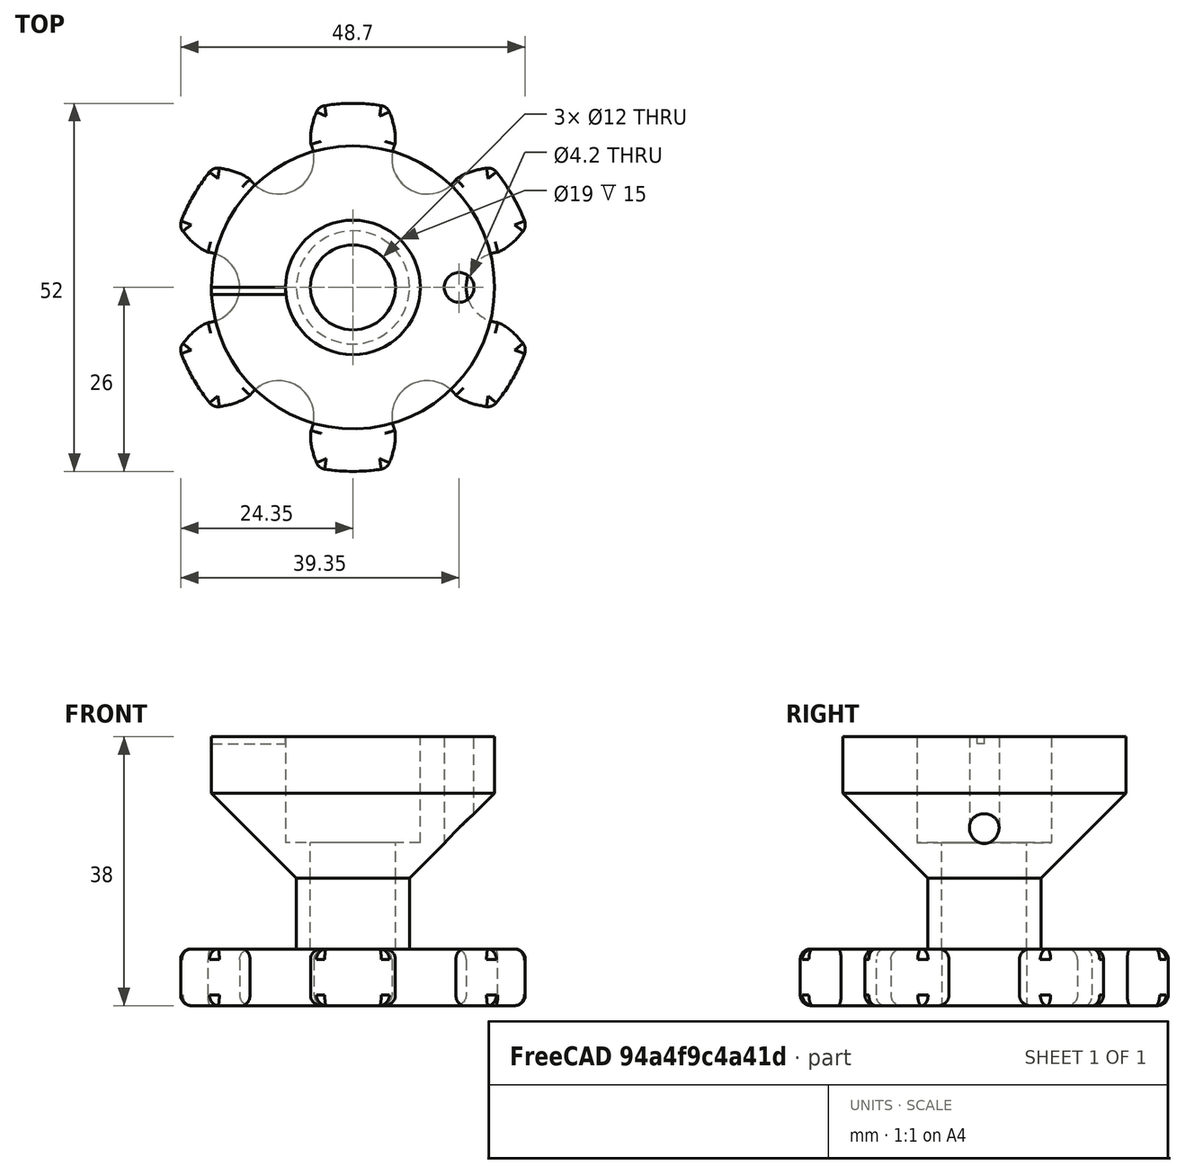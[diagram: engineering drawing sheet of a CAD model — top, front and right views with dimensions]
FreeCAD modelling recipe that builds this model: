
FCSTD DOCUMENT  (FreeCAD 0.21R33771 (Git))
Label: sprocket
License: Public Domain
LicenseURL: https://en.wikipedia.org/wiki/Public_domain
objects: PartDesign::Line×6, Part::Cut×5, Part::FeaturePython×3, Part::Cylinder×3, PartDesign::CoordinateSystem×2, Part::MultiFuse×2, Part::Box×1, Part::Chamfer×1, Part::Fillet×1, App::Part×1
note: 24 computed .brp shape members not serialized (recipe doc carries the construction recipe); baked Part::Feature solids carry a one-line shape summary decoded from their .brp

FEATURE [Part::FeaturePython] LanternGear  # WARN: FeaturePython — macro-defined, semantics opaque (R4)
  AttacherType = Attacher::AttachEngine3D
  bolt_radius = 5
  head = 0
  height = 8
  module = 7
  num_profiles = 10
  teeth = 6
  version = 1.2.0
FEATURE [PartDesign::CoordinateSystem] LCS_Origin  label="Axle AP"
  AttacherType = Attacher::AttachEngine3D
  MapMode = 2
  Support = -> [X_Axis]
FEATURE [Part::Box] Box  label="Indicator cutter"
  AttacherType = Attacher::AttachEngine3D
  Height = 1
  Length = 1
  Placement = pos=(-20,2e-15,37) rot=(0,0,-1;1.5708rad)
  Width = 10.5
  expr: .Placement.Base.x = 0 mm - <<mount  top tube>>.OuterRadius
  expr: .Placement.Base.z = <<mount  top tube>>.Placement.Base.z + <<mount  top tube>>.Height - Height
  expr: Width = <<mount  top tube>>.OuterRadius - <<Bearing hole cutter>>.Radius
FEATURE [Part::FeaturePython] Tube  label="mount base"  # WARN: FeaturePython — macro-defined, semantics opaque (R4)
  AttacherType = Attacher::AttachEngine3D
  Height = 10
  InnerRadius = 6
  OuterRadius = 8
  Placement = pos=(0,0,8) rot=(0,0,1;0rad)
  expr: .Placement.Base.z = LanternGear.height
FEATURE [Part::FeaturePython] Tube001  label="mount  top tube"  # WARN: FeaturePython — macro-defined, semantics opaque (R4)
  AttacherType = Attacher::AttachEngine3D
  Height = 20
  InnerRadius = 6
  OuterRadius = 20
  Placement = pos=(0,0,18) rot=(0,0,1;0rad)
  expr: .Placement.Base.z = <<mount base>>.Placement.Base.z + <<mount base>>.Height
FEATURE [Part::Cylinder] Cylinder  label="cam axle cutter"
  Angle = 360
  AttacherType = Attacher::AttachEngine3D
  FirstAngle = 0
  Height = 20
  Placement = pos=(15,0,18) rot=(0,0,1;0rad)
  Radius = 2.1
  SecondAngle = 0
  expr: .Placement.Base.z = <<mount  top tube>>.Placement.Base.z
  expr: Height = <<mount  top tube>>.Height
FEATURE [Part::Cylinder] Cylinder001  label="Bearing hole cutter"
  Angle = 360
  AttacherType = Attacher::AttachEngine3D
  FirstAngle = 0
  Height = 15
  Placement = pos=(0,0,23) rot=(0,0,1;0rad)
  Radius = 9.5
  SecondAngle = 0
FEATURE [Part::Cylinder] Cylinder002  label="sprocket hole"
  Angle = 360
  AttacherType = Attacher::AttachEngine3D
  FirstAngle = 0
  Height = 18
  Radius = 6
  SecondAngle = 0
  expr: Height = <<mount base>>.Height + LanternGear.height
FEATURE [Part::Cut] Cut  label="sprocket w axle hole"
  Base = -> LanternGear
  Tool = -> Cylinder002
FEATURE [Part::Cut] Cut004  label="mount base w axle hole"
  Base = -> Tube
  Tool = -> Cylinder002
FEATURE [Part::Chamfer] Chamfer
  Base = -> Tube001
  Edges = 1 edges r=12: [Edge3]
FEATURE [Part::Cut] Cut005
  Base = -> Chamfer
  Tool = -> Cylinder001
FEATURE [Part::Cut] Cut006
  Base = -> Cut005
  Tool = -> Cylinder
FEATURE [Part::Cut] Cut007  label="Mount Top"
  Base = -> Cut006
  Tool = -> Box
FEATURE [Part::MultiFuse] Fusion  label="Cam Mount"
  Shapes = -> [Cut004,Cut007]
FEATURE [Part::MultiFuse] Fusion001  label="Unfinished Sprocket"
  Shapes = -> [Cut,Fusion]
FEATURE [PartDesign::CoordinateSystem] Roller_AP  label="Roller AP 1"
  AttacherType = Attacher::AttachEngine3D
  AttachmentOffset = pos=(0,0,4) rot=(0,0,1;0rad)
  MapMode = 11
  Placement = pos=(10.5,-18.1865,4) rot=(0,0,1;2.20035rad)
  Support = -> [Fusion001]
  expr: .AttachmentOffset.Base.z = LanternGear.height / 2
FEATURE [PartDesign::Line] HoleAxis_1  label="Cam Axle AP"
  AttacherType = Attacher::AttachEngineLine
  Length = 6.76352
  MapMode = 19
  Placement = pos=(15,0,38) rot=(0,0,1;0rad)
  ResizeMode = 1
  Support = -> [Fusion001]
FEATURE [Part::Fillet] Fillet  label="Filleted Sprocket"
  Base = -> Fusion001
  Edges = 60 edges r=1.5: [Edge2,Edge3,Edge4,Edge6,Edge7,Edge8,Edge9,Edge10,Edge11,Edge12,Edge13,Edge14,Edge15,Edge16,Edge17,Edge18,Edge19,Edge20,Edge21,Edge22,Edge23,Edge24,Edge25,Edge26,Edge27,Edge28,Edge29,Edge30,Edge31,Edge33,Edge34,Edge35,Edge36,Edge37,Edge38,Edge39,Edge40,Edge41,Edge42,Edge43,Edge44,Edge45,Edge46,+17 more]
FEATURE [PartDesign::Line] HoleAxis_2  label="Roller AP 2"
  AttacherType = Attacher::AttachEngineLine
  AttachmentOffset = pos=(0,0,4) rot=(0,0,1;0rad)
  Length = 10.9029
  MapMode = 19
  Placement = pos=(21,-1.5e-15,4) rot=(0,0,1;1.67675rad)
  ResizeMode = 1
  Support = -> [Fusion001]
  expr: .AttachmentOffset.Base.z = LanternGear.height / 2
FEATURE [PartDesign::Line] HoleAxis_3  label="Roller AP 3"
  AttacherType = Attacher::AttachEngineLine
  AttachmentOffset = pos=(0,0,4) rot=(0,0,1;0rad)
  Length = 5.91808
  MapMode = 19
  Placement = pos=(10.5,18.1865,4) rot=(0,0,1;2.72395rad)
  ResizeMode = 1
  Support = -> [Fusion001]
  expr: .AttachmentOffset.Base.z = LanternGear.height / 2
FEATURE [PartDesign::Line] HoleAxis_4  label="Roller AP 4"
  AttacherType = Attacher::AttachEngineLine
  AttachmentOffset = pos=(0,0,4) rot=(0,0,1;0rad)
  Length = 21.2118
  MapMode = 19
  Placement = pos=(-10.5,18.1865,4) rot=(0,0,1;3.77115rad)
  ResizeMode = 1
  Support = -> [Fusion001]
  expr: .AttachmentOffset.Base.z = LanternGear.height / 2
FEATURE [PartDesign::Line] HoleAxis_5  label="Roller AP 5"
  AttacherType = Attacher::AttachEngineLine
  AttachmentOffset = pos=(0,0,4) rot=(0,0,1;0rad)
  Length = 21.2118
  MapMode = 19
  Placement = pos=(-21,1.2e-14,4) rot=(0,0,-1;1.46484rad)
  ResizeMode = 1
  Support = -> [Fusion001]
  expr: .AttachmentOffset.Base.z = LanternGear.height / 2
FEATURE [PartDesign::Line] HoleAxis_6  label="Roller AP 6"
  AttacherType = Attacher::AttachEngineLine
  AttachmentOffset = pos=(0,0,4) rot=(0,0,1;0rad)
  Length = 44.6718
  MapMode = 19
  Placement = pos=(-10.5,-18.1865,4) rot=(0,0,-1;0.41764rad)
  ResizeMode = 1
  Support = -> [Fusion001]
  expr: .AttachmentOffset.Base.z = LanternGear.height / 2
FEATURE [App::Part] Sprocket
  Group = -> [LCS_Origin,Roller_AP,HoleAxis_1,LanternGear,Box,Tube001,Cylinder,Cylinder001,Tube,Cut007,Cut005,Cut006,Fusion,Cylinder002,Cut,Cut004,Chamfer,Fusion001,Fillet,HoleAxis_2,HoleAxis_3,HoleAxis_4,HoleAxis_5,HoleAxis_6]
  Origin = -> Origin
